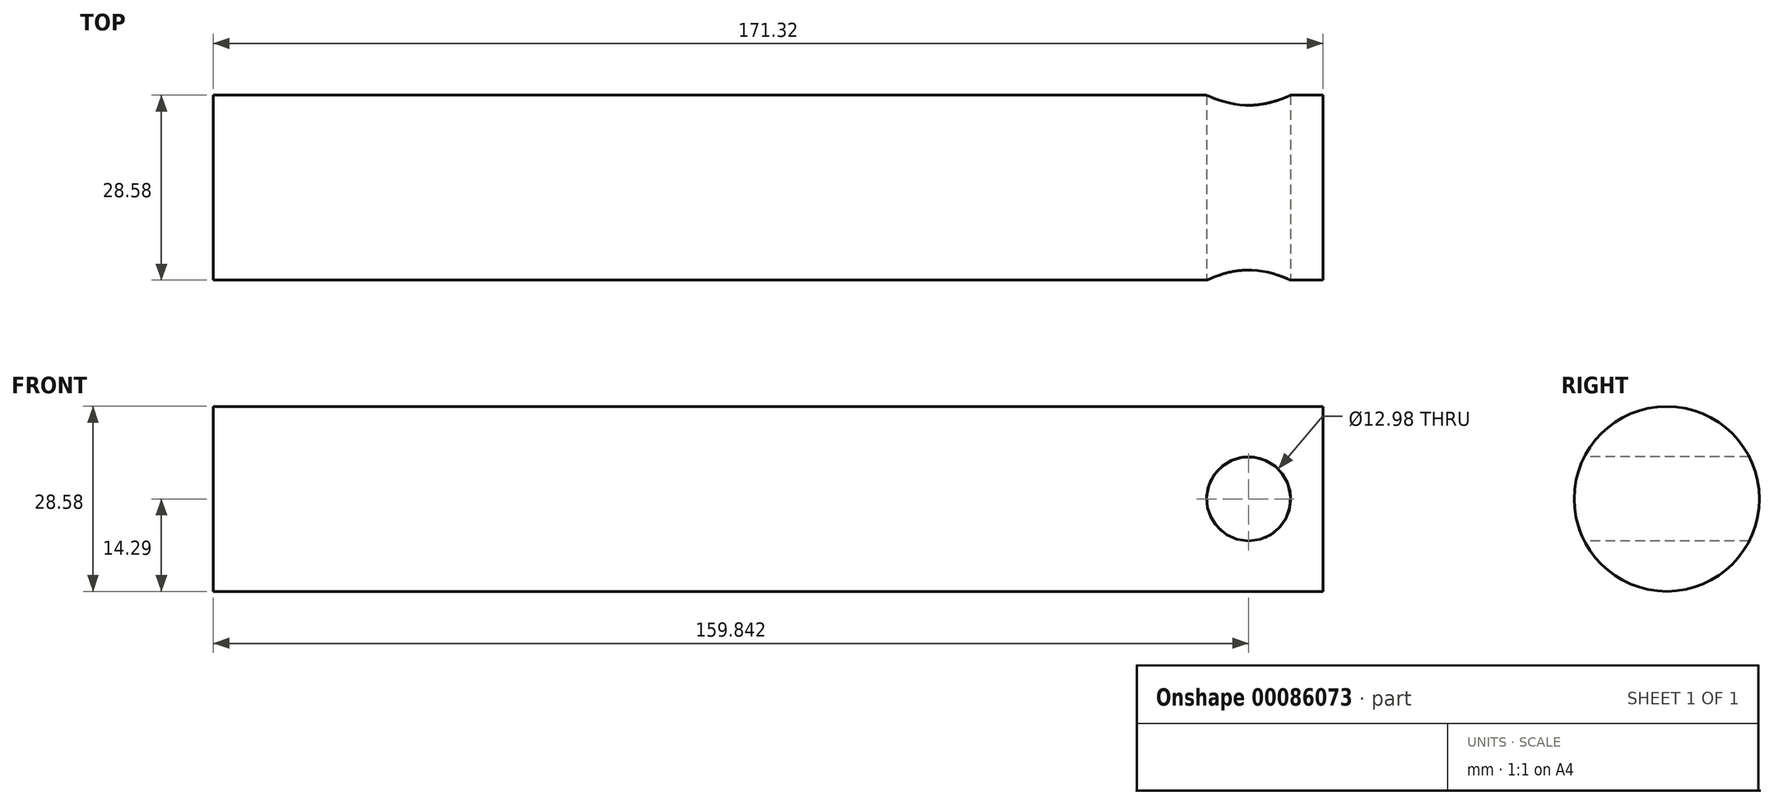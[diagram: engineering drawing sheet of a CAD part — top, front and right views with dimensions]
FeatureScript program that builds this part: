
annotation { "Feature Type Name" : "Feature", "Feature Type Description" : "" }
export const myFeature = defineFeature(function(context is Context, id is Id, definition is map)
    precondition{}
    {
        {
            var Q0;
            Q0=qCreatedBy(makeId("Right.planeOp"),FACE);
            var sketch = newSketch(context, id + "F0", { "sketchPlane" : qUnion([Q0])});
            skCircle(sketch, "E0", {"center": v(0, 0) * mm, "radius": 14.29 * mm});
            skSolve(sketch);
        }
        {
            var Q0;
            Q0=makeQuery(id+"F0.imprint","IMPRINT",FACE,{"disambiguationData":[TD([[makeQuery(id+"F0.imprint","IMPRINT",EDGE,{"derivedFrom":sQuery(id+"F0.wireOp",EDGE,"E0")}),1.0]])]});
            extrude(context, id + "F1", {"entities" : qUnion([Q0]), "depth" : 171.32 * mm});
        }
        {
            var Q0;
            Q0=qCreatedBy(makeId("Front.planeOp"),FACE);
            var sketch = newSketch(context, id + "F2", { "sketchPlane" : qUnion([Q0])});
            skCircle(sketch, "E1", {"center": v(159.84, 0) * mm, "radius": 6.49 * mm});
            skSolve(sketch);
        }
        {
            var Q0;
            Q0 = qSketchRegion(id + "F2", true);
            extrude(context, id + "F3", {"entities" : qUnion([Q0]), "operationType" : NewBodyOperationType.REMOVE, "endBound" : BoundingType.SYMMETRIC, "oppositeDirection" : true, "depth" : 50.8 * mm});
        }
    });
